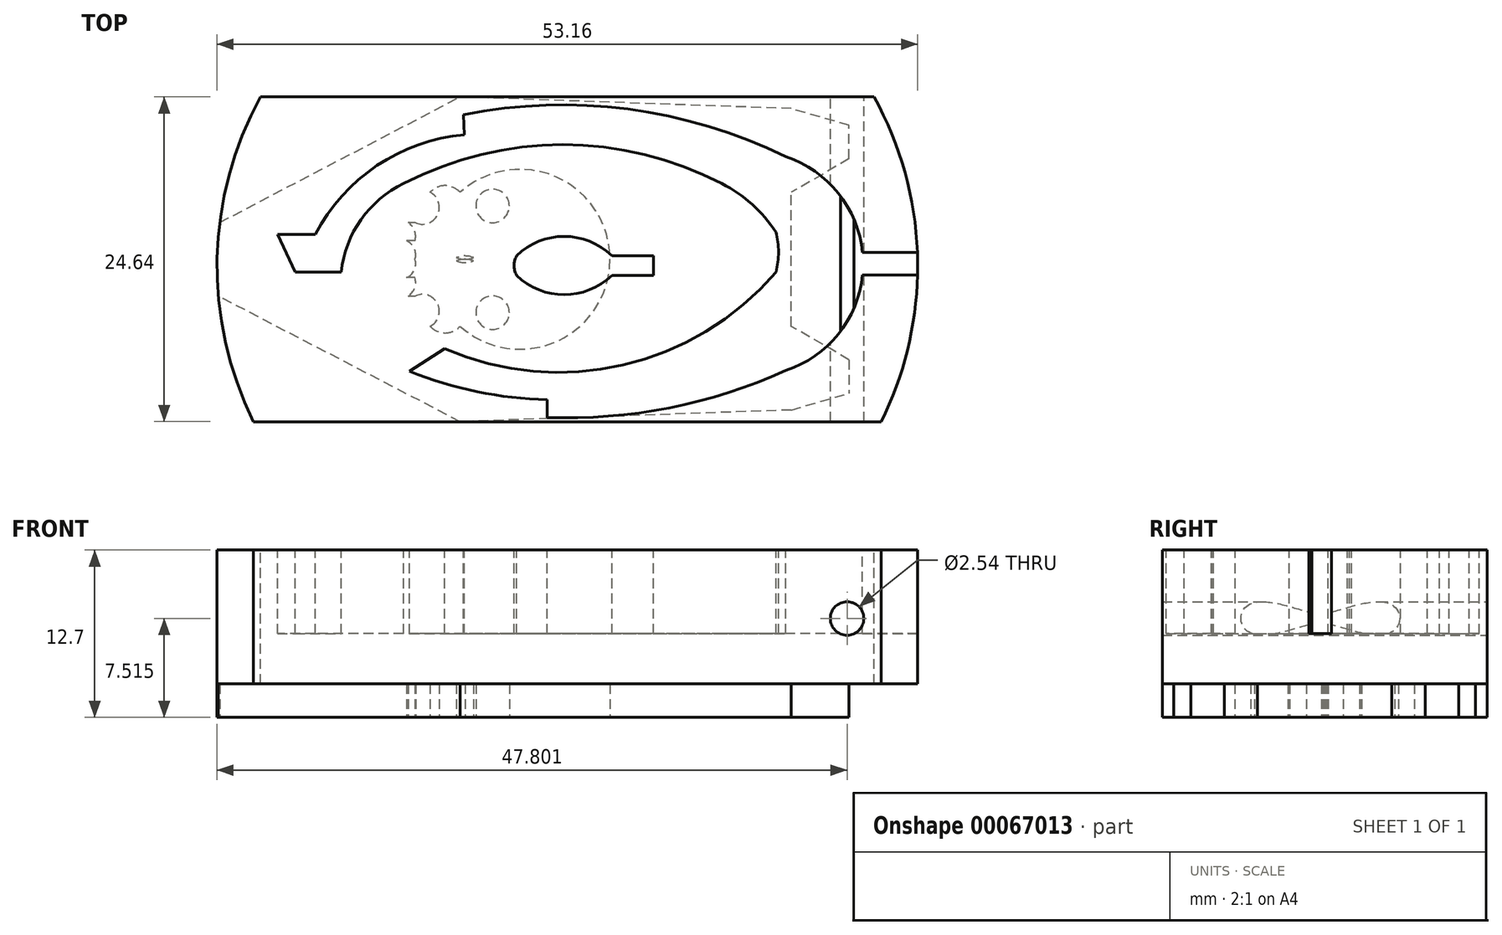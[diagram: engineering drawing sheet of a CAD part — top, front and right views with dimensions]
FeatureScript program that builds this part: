
annotation { "Feature Type Name" : "Feature", "Feature Type Description" : "" }
export const myFeature = defineFeature(function(context is Context, id is Id, definition is map)
    precondition{}
    {
        {
            var Q0;
            Q0=qCreatedBy(makeId("Top.planeOp"),FACE);
            var sketch = newSketch(context, id + "F0", { "sketchPlane" : qUnion([Q0])});
            skCircle(sketch, "E0", {"center": v(38.34, 21.8) * mm, "radius": 26.58 * mm});
            skSolve(sketch);
        }
        {
            var Q0;
            Q0 = qSketchRegion(id + "F0", true);
            extrude(context, id + "F1", {"entities" : qUnion([Q0]), "depth" : 12.7 * mm});
        }
        {
            var Q0;
            Q0=makeQuery(id+"F1.opExtrude","CAP_FACE",FACE,{"disambiguationData":[OSD([sQuery(id+"F0.wireOp",EDGE,"E0")])],"isStart":false});
            var sketch = newSketch(context, id + "F2", { "sketchPlane" : qUnion([Q0])});
            skPoint(sketch, "E1", {"position": v(64.9, 21.22) * mm});
            skPoint(sketch, "E2", {"position": v(64.9, 22.85) * mm});
            skPoint(sketch, "E3", {"position": v(64.91, 21.87) * mm});
            skArc(sketch, "E4", {"start": v(64.9, 21.22) * mm, "mid": v(64.91, 22.04) * mm, "end": v(64.9, 22.85) * mm});
            skPoint(sketch, "E5", {"position": v(60.91, 21.22) * mm});
            skPoint(sketch, "E6", {"position": v(60.91, 22.85) * mm});
            skPoint(sketch, "E7", {"position": v(41.71, 22.58) * mm});
            skPoint(sketch, "E8", {"position": v(41.71, 21.1) * mm});
            skPoint(sketch, "E9", {"position": v(34.49, 21.1) * mm});
            skPoint(sketch, "E10", {"position": v(34.49, 22.58) * mm});
            skArc(sketch, "E11", {"start": v(41.71, 22.58) * mm, "mid": v(38.1, 24.05) * mm, "end": v(34.49, 22.58) * mm});
            skArc(sketch, "E12", {"start": v(34.49, 21.1) * mm, "mid": v(38.1, 19.63) * mm, "end": v(41.71, 21.1) * mm});
            skArc(sketch, "E13", {"start": v(34.49, 22.58) * mm, "mid": v(34.3, 21.84) * mm, "end": v(34.49, 21.1) * mm});
            skPoint(sketch, "E14", {"position": v(44.87, 22.58) * mm});
            skPoint(sketch, "E15", {"position": v(44.87, 21.1) * mm});
            skLineSegment(sketch, "E16", {"start": v(41.71, 22.58) * mm, "end": v(44.87, 22.58) * mm});
            skLineSegment(sketch, "E17", {"start": v(44.87, 21.1) * mm, "end": v(44.87, 22.58) * mm});
            skLineSegment(sketch, "E18", {"start": v(44.87, 21.1) * mm, "end": v(41.71, 21.1) * mm});
            skSolve(sketch);
        }
        {
            var Q0;
            Q0 = qSketchRegion(id + "F2", true);
            extrude(context, id + "F3", {"entities" : qUnion([Q0]), "operationType" : NewBodyOperationType.REMOVE, "oppositeDirection" : true, "depth" : 6.35 * mm});
        }
        {
            var Q0;
            Q0=makeQuery(id+"F1.opExtrude","CAP_FACE",FACE,{"disambiguationData":[OSD([sQuery(id+"F0.wireOp",EDGE,"E0")])],"isStart":false});
            var sketch = newSketch(context, id + "F4", { "sketchPlane" : qUnion([Q0])});
            skPoint(sketch, "E19", {"position": v(30.46, 33.3) * mm});
            skPoint(sketch, "E20", {"position": v(30.52, 31.77) * mm});
            skLineSegment(sketch, "E21", {"start": v(30.52, 31.77) * mm, "end": v(30.46, 33.3) * mm});
            skArc(sketch, "E22", {"start": v(30.52, 31.77) * mm, "mid": v(23.9, 29.43) * mm, "end": v(19.22, 24.2) * mm});
            skPoint(sketch, "E23", {"position": v(16.35, 24.2) * mm});
            skPoint(sketch, "E24", {"position": v(21.19, 21.35) * mm});
            skPoint(sketch, "E25", {"position": v(17.68, 21.35) * mm});
            skLineSegment(sketch, "E26", {"start": v(19.22, 24.2) * mm, "end": v(16.35, 24.2) * mm});
            skLineSegment(sketch, "E27", {"start": v(17.68, 21.35) * mm, "end": v(21.19, 21.35) * mm});
            skLineSegment(sketch, "E28", {"start": v(16.35, 24.2) * mm, "end": v(17.68, 21.35) * mm});
            skPoint(sketch, "E29", {"position": v(54.16, 21.35) * mm});
            skArc(sketch, "E30", {"start": v(29.03, 15.53) * mm, "mid": v(42.56, 14.29) * mm, "end": v(54.16, 21.35) * mm});
            skArc(sketch, "E31", {"start": v(54.16, 21.35) * mm, "mid": v(54.36, 22.86) * mm, "end": v(54.16, 24.38) * mm});
            skPoint(sketch, "E32", {"position": v(29.03, 15.53) * mm});
            skPoint(sketch, "E33", {"position": v(26.37, 13.8) * mm});
            skPoint(sketch, "E34", {"position": v(36.8, 11.66) * mm});
            skPoint(sketch, "E35", {"position": v(36.8, 10.31) * mm});
            skLineSegment(sketch, "E36", {"start": v(29.03, 15.53) * mm, "end": v(26.37, 13.8) * mm});
            skArc(sketch, "E37", {"start": v(26.37, 13.8) * mm, "mid": v(31.5, 12.27) * mm, "end": v(36.8, 11.66) * mm});
            skPoint(sketch, "E38", {"position": v(54.9, 30.1) * mm});
            skArc(sketch, "E39", {"start": v(54.9, 30.1) * mm, "mid": v(42.95, 33.71) * mm, "end": v(30.46, 33.3) * mm});
            skPoint(sketch, "E40", {"position": v(54.9, 13.88) * mm});
            skArc(sketch, "E41", {"start": v(36.8, 10.31) * mm, "mid": v(46.06, 11.04) * mm, "end": v(54.9, 13.88) * mm});
            skLineSegment(sketch, "E42", {"start": v(36.8, 11.66) * mm, "end": v(36.8, 10.31) * mm});
            skArc(sketch, "E43", {"start": v(54.9, 13.88) * mm, "mid": v(58.9, 16.64) * mm, "end": v(60.73, 21.14) * mm});
            skPoint(sketch, "E44", {"position": v(60.73, 22.83) * mm});
            skPoint(sketch, "E45", {"position": v(60.73, 21.14) * mm});
            skArc(sketch, "E46.trimOffspring", {"start": v(60.73, 22.83) * mm, "mid": v(58.9, 27.33) * mm, "end": v(54.9, 30.1) * mm});
            skPoint(sketch, "E47", {"position": v(64.9, 22.83) * mm});
            skPoint(sketch, "E48", {"position": v(64.9, 21.14) * mm});
            skPoint(sketch, "E49", {"position": v(64.91, 21.97) * mm});
            skArc(sketch, "E50", {"start": v(64.9, 21.14) * mm, "mid": v(64.91, 21.99) * mm, "end": v(64.9, 22.83) * mm});
            skLineSegment(sketch, "E51", {"start": v(60.73, 22.83) * mm, "end": v(64.9, 22.83) * mm});
            skLineSegment(sketch, "E52", {"start": v(64.9, 21.14) * mm, "end": v(60.73, 21.14) * mm});
            skArc(sketch, "E53", {"start": v(25.93, 28.06) * mm, "mid": v(22.68, 25.33) * mm, "end": v(21.19, 21.35) * mm});
            skArc(sketch, "E54", {"start": v(50.06, 28.06) * mm, "mid": v(38, 31.02) * mm, "end": v(25.93, 28.06) * mm});
            skArc(sketch, "E55", {"start": v(54.16, 24.38) * mm, "mid": v(52.35, 26.49) * mm, "end": v(50.06, 28.06) * mm});
            skSolve(sketch);
        }
        {
            var Q0;
            Q0 = qSketchRegion(id + "F4", true);
            extrude(context, id + "F5", {"entities" : qUnion([Q0]), "operationType" : NewBodyOperationType.REMOVE, "oppositeDirection" : true, "depth" : 6.35 * mm});
        }
        {
            var Q0;
            Q0=makeQuery(id+"F1.opExtrude","CAP_FACE",FACE,{"disambiguationData":[OSD([sQuery(id+"F0.wireOp",EDGE,"E0")])],"isStart":false});
            var sketch = newSketch(context, id + "F6", { "sketchPlane" : qUnion([Q0])});
            skLineSegment(sketch, "E56", {"start": v(36.8, 10) * mm, "end": v(62.15, 10) * mm});
            skLineSegment(sketch, "E57", {"start": v(62.15, 10) * mm, "end": v(14.53, 10) * mm});
            skLineSegment(sketch, "E58", {"start": v(14.53, 10) * mm, "end": v(36.8, 10) * mm});
            skLineSegment(sketch, "E59", {"start": v(38.57, 34.64) * mm, "end": v(61.6, 34.64) * mm});
            skLineSegment(sketch, "E60", {"start": v(61.6, 34.64) * mm, "end": v(15.07, 34.64) * mm});
            skLineSegment(sketch, "E61", {"start": v(15.07, 34.64) * mm, "end": v(38.57, 34.64) * mm});
            skPoint(sketch, "E62", {"position": v(39.59, 48.35) * mm});
            skPoint(sketch, "E63", {"position": v(39.5, -4.75) * mm});
            skArc(sketch, "E64", {"start": v(61.6, 34.64) * mm, "mid": v(38.34, 48.38) * mm, "end": v(15.07, 34.64) * mm});
            skArc(sketch, "E65", {"start": v(14.53, 10) * mm, "mid": v(38.34, -4.77) * mm, "end": v(62.15, 10) * mm});
            skSolve(sketch);
        }
        {
            var Q0;
            Q0 = qSketchRegion(id + "F6", true);
            extrude(context, id + "F7", {"entities" : qUnion([Q0]), "operationType" : NewBodyOperationType.REMOVE, "oppositeDirection" : true, "depth" : 25.4 * mm});
        }
        {
            var Q0;
            Q0=makeQuery(id+"F7.boolean.opBoolean","COPY",FACE,{"derivedFrom":makeQuery(id+"F7.opExtrude","SWEPT_FACE",FACE,{"disambiguationData":[OSD([sQuery(id+"F6.wireOp",EDGE,"E60"),sQuery(id+"F6.wireOp",EDGE,"E61")])]})});
            var sketch = newSketch(context, id + "F8", { "sketchPlane" : qUnion([Q0])});
            skPoint(sketch, "E66", {"position": v(-59.56, 7.51) * mm});
            skSolve(sketch);
        }
        {
            var Q0;
            Q0=sQuery(id+"F8.wireOp",VERTEX,"E66");
            var Q1;
            Q1=makeQuery(id+"F1.opExtrude","SWEPT_BODY",BODY,{"disambiguationData":[OSD([sQuery(id+"F0.wireOp",EDGE,"E0")])]});
            hole(context, id + "F9", {"style" : HoleStyle.SIMPLE, "holeDiameter" : 2.54 * mm, "endStyle" : HoleEndStyle.THROUGH, "locations" : qUnion([Q0]), "scope" : qUnion([Q1])});
        }
        {
            var Q0;
            Q0=makeQuery(id+"F1.opExtrude","CAP_FACE",FACE,{"disambiguationData":[OSD([sQuery(id+"F0.wireOp",EDGE,"E0")])],"isStart":true});
            var sketch = newSketch(context, id + "F10", { "sketchPlane" : qUnion([Q0])});
            skPoint(sketch, "E67", {"position": v(59.71, -12.16) * mm});
            skPoint(sketch, "E68", {"position": v(59.71, -32.48) * mm});
            skPoint(sketch, "E69", {"position": v(59.71, -14.7) * mm});
            skPoint(sketch, "E70", {"position": v(59.71, -29.94) * mm});
            skPoint(sketch, "E71", {"position": v(55.33, -14.7) * mm});
            skPoint(sketch, "E72", {"position": v(55.33, -29.94) * mm});
            skPoint(sketch, "E73", {"position": v(55.33, -17.24) * mm});
            skPoint(sketch, "E74", {"position": v(55.33, -27.4) * mm});
            skLineSegment(sketch, "E75", {"start": v(59.71, -14.7) * mm, "end": v(55.33, -17.24) * mm});
            skLineSegment(sketch, "E76", {"start": v(55.33, -17.24) * mm, "end": v(55.33, -27.4) * mm});
            skLineSegment(sketch, "E77", {"start": v(59.71, -29.94) * mm, "end": v(55.33, -27.4) * mm});
            skPoint(sketch, "E78", {"position": v(55.33, -32.48) * mm});
            skPoint(sketch, "E79", {"position": v(55.33, -12.16) * mm});
            skPoint(sketch, "E80", {"position": v(55.33, -33.75) * mm});
            skPoint(sketch, "E81", {"position": v(55.33, -10.89) * mm});
            skLineSegment(sketch, "E82", {"start": v(59.71, -14.7) * mm, "end": v(59.71, -12.16) * mm});
            skLineSegment(sketch, "E83", {"start": v(55.33, -10.89) * mm, "end": v(59.71, -12.16) * mm});
            skLineSegment(sketch, "E84", {"start": v(59.71, -29.94) * mm, "end": v(59.71, -32.48) * mm});
            skLineSegment(sketch, "E85", {"start": v(59.71, -32.48) * mm, "end": v(55.33, -33.75) * mm});
            skPoint(sketch, "E86", {"position": v(30.2, -10) * mm});
            skPoint(sketch, "E87", {"position": v(30.2, -34.64) * mm});
            skLineSegment(sketch, "E88", {"start": v(55.33, -10.89) * mm, "end": v(30.2, -10) * mm});
            skLineSegment(sketch, "E89", {"start": v(55.33, -33.75) * mm, "end": v(30.2, -34.64) * mm});
            skPoint(sketch, "E90", {"position": v(30.2, -17.24) * mm});
            skPoint(sketch, "E91", {"position": v(30.2, -27.4) * mm});
            skArc(sketch, "E92", {"start": v(30.2, -27.4) * mm, "mid": v(41.58, -22.32) * mm, "end": v(30.2, -17.24) * mm});
            skPoint(sketch, "E93", {"position": v(27.92, -27.4) * mm});
            skPoint(sketch, "E94", {"position": v(27.92, -17.24) * mm});
            skPoint(sketch, "E95", {"position": v(64.8, -88.19) * mm});
            skLineSegment(sketch, "E96", {"start": v(30.2, -17.24) * mm, "end": v(27.92, -17.24) * mm});
            skLineSegment(sketch, "E97", {"start": v(30.2, -27.4) * mm, "end": v(27.92, -27.4) * mm});
            skPoint(sketch, "E98", {"position": v(29.06, -27.9) * mm});
            skPoint(sketch, "E98.positionSnap0", {"position": v(29.06, -27.4) * mm});
            skPoint(sketch, "E99", {"position": v(29.06, -16.73) * mm});
            skPoint(sketch, "E99.positionSnap0", {"position": v(29.06, -17.24) * mm});
            skArc(sketch, "E100", {"start": v(30.2, -17.24) * mm, "mid": v(29.06, -16.73) * mm, "end": v(27.92, -17.24) * mm});
            skArc(sketch, "E101", {"start": v(27.92, -27.4) * mm, "mid": v(29.06, -27.9) * mm, "end": v(30.2, -27.4) * mm});
            skPoint(sketch, "E102", {"position": v(27.92, -19.52) * mm});
            skPoint(sketch, "E103", {"position": v(27.92, -25.11) * mm});
            skPoint(sketch, "E104", {"position": v(26.78, -19.52) * mm});
            skPoint(sketch, "E105", {"position": v(26.78, -25.11) * mm});
            skArc(sketch, "E106", {"start": v(26.78, -19.52) * mm, "mid": v(28.5, -18.95) * mm, "end": v(27.92, -17.24) * mm});
            skArc(sketch, "E107", {"start": v(27.92, -27.4) * mm, "mid": v(28.5, -25.69) * mm, "end": v(26.78, -25.11) * mm});
            skPoint(sketch, "E108", {"position": v(26.78, -22.32) * mm});
            skPoint(sketch, "E109", {"position": v(26.78, -23.72) * mm});
            skPoint(sketch, "E110", {"position": v(26.78, -20.92) * mm});
            skPoint(sketch, "E111", {"position": v(26.27, -19.52) * mm});
            skPoint(sketch, "E112", {"position": v(25.24, -20.92) * mm});
            skPoint(sketch, "E113", {"position": v(26.52, -22.32) * mm});
            skPoint(sketch, "E114", {"position": v(25.24, -23.72) * mm});
            skPoint(sketch, "E115", {"position": v(26.27, -25.11) * mm});
            skLineSegment(sketch, "E116", {"start": v(26.78, -19.52) * mm, "end": v(26.78, -20.92) * mm});
            skLineSegment(sketch, "E117", {"start": v(26.78, -20.92) * mm, "end": v(26.78, -22.32) * mm});
            skLineSegment(sketch, "E118", {"start": v(26.78, -22.32) * mm, "end": v(26.78, -23.72) * mm});
            skLineSegment(sketch, "E119", {"start": v(26.78, -23.72) * mm, "end": v(26.78, -25.11) * mm});
            skPoint(sketch, "E120", {"position": v(26.78, -20.22) * mm});
            skPoint(sketch, "E121", {"position": v(26.78, -21.62) * mm});
            skPoint(sketch, "E122", {"position": v(26.78, -23.02) * mm});
            skPoint(sketch, "E123", {"position": v(26.78, -24.41) * mm});
            skArc(sketch, "E124", {"start": v(26.78, -20.92) * mm, "mid": v(26.75, -20.14) * mm, "end": v(26.27, -19.52) * mm});
            skArc(sketch, "E125", {"start": v(26.78, -22.32) * mm, "mid": v(26.73, -21.5) * mm, "end": v(26.14, -20.92) * mm});
            skArc(sketch, "E126", {"start": v(26.14, -23.72) * mm, "mid": v(26.73, -23.14) * mm, "end": v(26.78, -22.32) * mm});
            skArc(sketch, "E127", {"start": v(26.27, -25.11) * mm, "mid": v(26.75, -24.5) * mm, "end": v(26.78, -23.72) * mm});
            skLineSegment(sketch, "E128", {"start": v(26.78, -20.92) * mm, "end": v(26.14, -20.92) * mm});
            skLineSegment(sketch, "E129", {"start": v(26.78, -23.72) * mm, "end": v(26.14, -23.72) * mm});
            skLineSegment(sketch, "E130", {"start": v(26.78, -19.52) * mm, "end": v(26.27, -19.52) * mm});
            skLineSegment(sketch, "E131", {"start": v(26.27, -25.11) * mm, "end": v(26.78, -25.11) * mm});
            skPoint(sketch, "E132", {"position": v(29.91, -22.32) * mm});
            skPoint(sketch, "E133", {"position": v(31.24, -22.32) * mm});
            skPoint(sketch, "E134", {"position": v(31.24, -22.44) * mm});
            skPoint(sketch, "E135", {"position": v(31.24, -22.2) * mm});
            skPoint(sketch, "E136", {"position": v(29.91, -22.44) * mm});
            skPoint(sketch, "E137", {"position": v(29.91, -22.2) * mm});
            skLineSegment(sketch, "E138", {"start": v(30.58, -22.32) * mm, "end": v(30.57, -22.32) * mm});
            skPoint(sketch, "E139", {"position": v(30.57, -22.32) * mm});
            skArc(sketch, "E140", {"start": v(29.91, -22.2) * mm, "mid": v(30.57, -22.32) * mm, "end": v(31.24, -22.2) * mm});
            skArc(sketch, "E141", {"start": v(31.24, -22.44) * mm, "mid": v(30.57, -22.32) * mm, "end": v(29.91, -22.44) * mm});
            skPoint(sketch, "E142", {"position": v(30.57, -22.44) * mm});
            skPoint(sketch, "E143", {"position": v(30.57, -22.2) * mm});
            skPoint(sketch, "E144", {"position": v(30.57, -22.57) * mm});
            skPoint(sketch, "E145", {"position": v(30.57, -22.06) * mm});
            skArc(sketch, "E146", {"start": v(31.24, -22.2) * mm, "mid": v(30.57, -22.06) * mm, "end": v(29.91, -22.2) * mm});
            skArc(sketch, "E147", {"start": v(29.91, -22.44) * mm, "mid": v(30.57, -22.57) * mm, "end": v(31.24, -22.44) * mm});
            skPoint(sketch, "E148.orphan", {"position": v(31.23, -22.32) * mm});
            skPoint(sketch, "E149", {"position": v(34.76, -24.1) * mm});
            skPoint(sketch, "E150", {"position": v(34.76, -20.54) * mm});
            skLineSegment(sketch, "E151", {"start": v(34.76, -20.54) * mm, "end": v(30.57, -20.54) * mm});
            skLineSegment(sketch, "E152", {"start": v(30.57, -24.1) * mm, "end": v(34.76, -24.1) * mm});
            skPoint(sketch, "E153", {"position": v(32.67, -26.37) * mm});
            skPoint(sketch, "E153.positionSnap0", {"position": v(32.67, -24.1) * mm});
            skPoint(sketch, "E154", {"position": v(32.67, -18.27) * mm});
            skPoint(sketch, "E154.positionSnap0", {"position": v(32.67, -20.54) * mm});
            skPoint(sketch, "E155", {"position": v(32.67, -17) * mm});
            skPoint(sketch, "E156", {"position": v(32.67, -27.64) * mm});
            skCircle(sketch, "E157", {"center": v(32.67, -18.27) * mm, "radius": 1.27 * mm});
            skCircle(sketch, "E158", {"center": v(32.67, -26.37) * mm, "radius": 1.27 * mm});
            skPoint(sketch, "E159", {"position": v(11.86, -19.52) * mm});
            skPoint(sketch, "E160", {"position": v(11.97, -25.11) * mm});
            skLineSegment(sketch, "E161", {"start": v(30.2, -10) * mm, "end": v(11.86, -19.52) * mm});
            skLineSegment(sketch, "E162", {"start": v(11.97, -25.11) * mm, "end": v(11.86, -19.52) * mm});
            skLineSegment(sketch, "E163", {"start": v(11.97, -25.11) * mm, "end": v(30.2, -34.64) * mm});
            skSolve(sketch);
        }
        {
            var Q0;
            {var subQ0=sQuery(id+"F10.wireOp",EDGE,"E161");Q0=makeQuery(id+"F10.imprint","IMPRINT",FACE,{"disambiguationData":[TD([[makeQuery(id+"F10.imprint","IMPRINT",EDGE,{"derivedFrom":subQ0}),-1.0]])]});}
            var Q1;
            {var subQ0=sQuery(id+"F10.wireOp",EDGE,"E163");Q1=makeQuery(id+"F10.imprint","IMPRINT",FACE,{"disambiguationData":[TD([[makeQuery(id+"F10.imprint","IMPRINT",EDGE,{"derivedFrom":subQ0}),-1.0]])]});}
            var Q2;
            Q2=makeQuery(id+"F10.imprint","IMPRINT",FACE,{"disambiguationData":[TD([[makeQuery(id+"F10.imprint","IMPRINT",EDGE,{"derivedFrom":sQuery(id+"F10.wireOp",EDGE,"E75")}),1.0]])]});
            var Q3;
            Q3=makeQuery(id+"F10.imprint","IMPRINT",FACE,{"disambiguationData":[TD([[makeQuery(id+"F10.imprint","IMPRINT",EDGE,{"derivedFrom":sQuery(id+"F10.wireOp",EDGE,"E92")}),1.0]])]});
            var Q4;
            Q4=makeQuery(id+"F10.imprint","IMPRINT",FACE,{"disambiguationData":[TD([[makeQuery(id+"F10.imprint","IMPRINT",EDGE,{"derivedFrom":sQuery(id+"F10.wireOp",EDGE,"E96")}),-1.0]])]});
            var Q5;
            Q5=makeQuery(id+"F10.imprint","IMPRINT",FACE,{"disambiguationData":[TD([[makeQuery(id+"F10.imprint","IMPRINT",EDGE,{"derivedFrom":sQuery(id+"F10.wireOp",EDGE,"E97")}),1.0]])]});
            var Q6;
            {var subQ0=sQuery(id+"F10.wireOp",EDGE,"E131");Q6=makeQuery(id+"F10.imprint","IMPRINT",FACE,{"disambiguationData":[TD([[makeQuery(id+"F10.imprint","IMPRINT",EDGE,{"derivedFrom":subQ0}),1.0]])]});}
            var Q7;
            {var subQ0=sQuery(id+"F10.wireOp",EDGE,"E129");Q7=makeQuery(id+"F10.imprint","IMPRINT",FACE,{"disambiguationData":[TD([[makeQuery(id+"F10.imprint","IMPRINT",EDGE,{"derivedFrom":subQ0}),-1.0]])]});}
            var Q8;
            {var subQ0=sQuery(id+"F10.wireOp",EDGE,"E128");Q8=makeQuery(id+"F10.imprint","IMPRINT",FACE,{"disambiguationData":[TD([[makeQuery(id+"F10.imprint","IMPRINT",EDGE,{"derivedFrom":subQ0}),1.0]])]});}
            var Q9;
            {var subQ0=sQuery(id+"F10.wireOp",EDGE,"E130");Q9=makeQuery(id+"F10.imprint","IMPRINT",FACE,{"disambiguationData":[TD([[makeQuery(id+"F10.imprint","IMPRINT",EDGE,{"derivedFrom":subQ0}),1.0]])]});}
            extrude(context, id + "F11", {"entities" : qUnion([Q0, Q1, Q2, Q3, Q4, Q5, Q6, Q7, Q8, Q9]), "operationType" : NewBodyOperationType.REMOVE, "oppositeDirection" : true, "depth" : 2.54 * mm});
        }
    });
